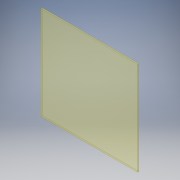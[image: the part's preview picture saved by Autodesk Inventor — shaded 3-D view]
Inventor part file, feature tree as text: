
AUTODESK INVENTOR PART (.ipt)
format: ipt  version: 2017 (Build 210142000, 142)  size: 94,720 bytes
history: native  units: in
note: dims shown in document units (in); Inventor stores cm internally (conversion verified against a paired STEP export)
features: extrude x1, sketch x1
ambient origin geometry x8: Origin, YZ Plane, XZ Plane, XY Plane, X Axis, Y Axis, Z Axis, Center Point
bodies: Solid1 (feature_tree)
feature tree (2):
  extrude  "Extrusion1"  Depth=8.5in
  sketch  "Sketch1"  dims[d0=8.787in d1=8.5in d2=0.125in d3=0.0in]
